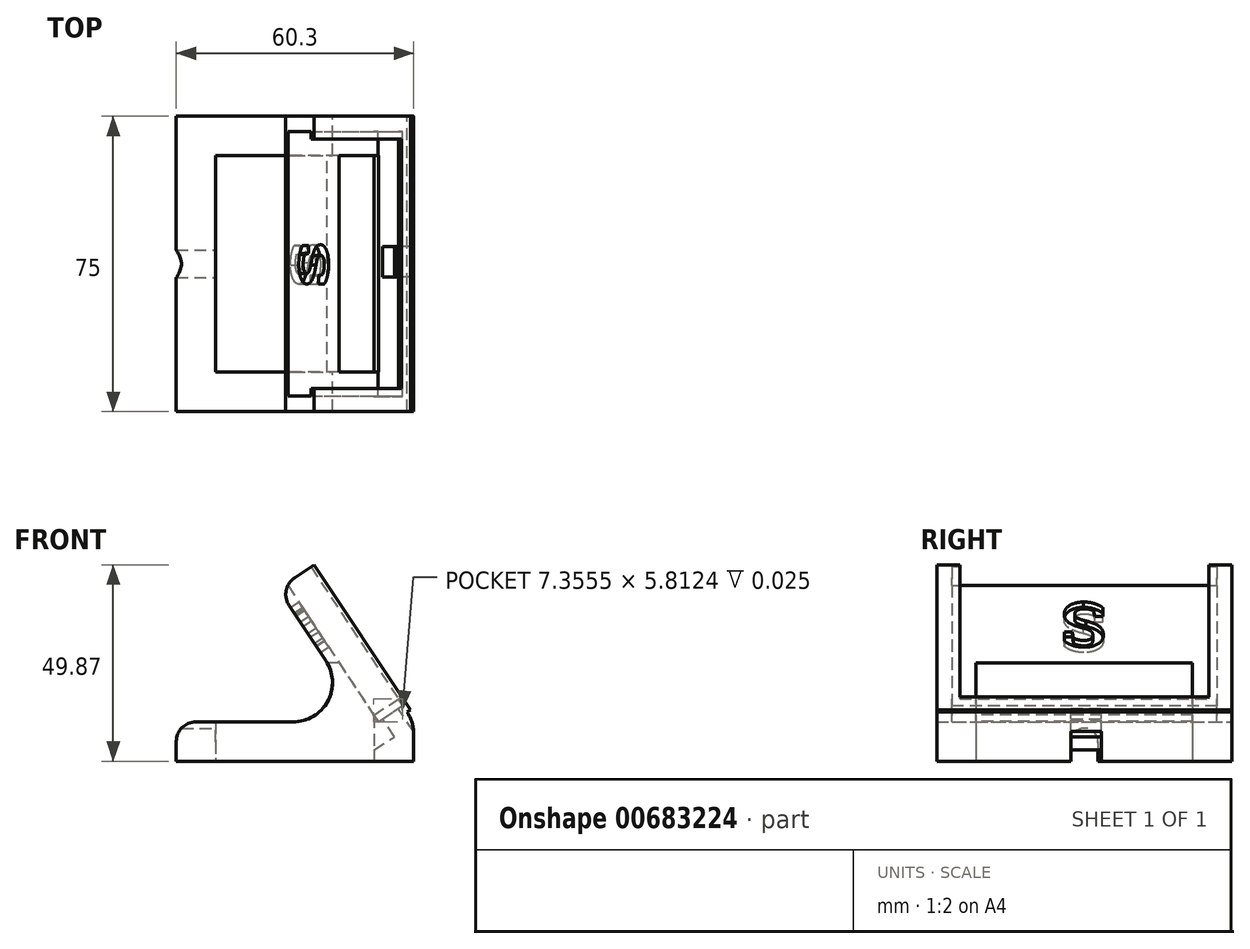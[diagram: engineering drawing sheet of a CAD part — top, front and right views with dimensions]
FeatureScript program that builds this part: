
annotation { "Feature Type Name" : "Feature", "Feature Type Description" : "" }
export const myFeature = defineFeature(function(context is Context, id is Id, definition is map)
    precondition{}
    {
        {
            var Q0;
            Q0=qCreatedBy(makeId("Front.planeOp"),FACE);
            var sketch = newSketch(context, id + "F0", { "sketchPlane" : qUnion([Q0])});
            skLineSegment(sketch, "E0", {"start": v(-43.3, 0) * mm, "end": v(-18.63, 0) * mm});
            skLineSegment(sketch, "E1", {"start": v(-10.3, 15.53) * mm, "end": v(-19.65, 29.62) * mm});
            skLineSegment(sketch, "E2", {"start": v(-18.25, 36.55) * mm, "end": v(-14.08, 39.32) * mm});
            skLineSegment(sketch, "E3", {"start": v(-14.08, 39.32) * mm, "end": v(10.33, 2.51) * mm});
            skLineSegment(sketch, "E4", {"start": v(12, -3.02) * mm, "end": v(12, -10) * mm});
            skLineSegment(sketch, "E5", {"start": v(12, -10) * mm, "end": v(-48.3, -10) * mm});
            skLineSegment(sketch, "E6", {"start": v(-48.3, -10) * mm, "end": v(-48.3, -5) * mm});
            skPoint(sketch, "E7.visualSharp", {"position": v(-48.3, 0) * mm});
            skArc(sketch, "E7.filletArc", {"start": v(-43.3, 0) * mm, "mid": v(-46.84, -1.46) * mm, "end": v(-48.3, -5) * mm});
            skPoint(sketch, "E8.visualSharp", {"position": v(12, 0) * mm});
            skArc(sketch, "E8.filletArc", {"start": v(12, -3.02) * mm, "mid": v(11.57, -0.13) * mm, "end": v(10.33, 2.51) * mm});
            skPoint(sketch, "E9.visualSharp", {"position": v(0, 0) * mm});
            skArc(sketch, "E9.filletArc", {"start": v(-18.63, 0) * mm, "mid": v(-9.82, 5.27) * mm, "end": v(-10.3, 15.53) * mm});
            skPoint(sketch, "E10.visualSharp", {"position": v(-22.41, 33.79) * mm});
            skArc(sketch, "E10.filletArc", {"start": v(-18.25, 36.55) * mm, "mid": v(-20.38, 33.38) * mm, "end": v(-19.65, 29.62) * mm});
            skSolve(sketch);
        }
        {
            var Q0;
            Q0 = qSketchRegion(id + "F0", true);
            extrude(context, id + "F1", {"entities" : qUnion([Q0]), "depth" : 75 * mm, "offsetDistance" : 25 * mm});
        }
        {
            var Q0;
            Q0=makeQuery(id+"F1.opExtrude","SWEPT_FACE",FACE,{"disambiguationData":[OSD([sQuery(id+"F0.wireOp",EDGE,"E3")])]});
            var sketch = newSketch(context, id + "F2", { "sketchPlane" : qUnion([Q0])});
            skLineSegment(sketch, "E11.bottom", {"start": v(-71.15, 60.38) * mm, "end": v(-3.85, 60.38) * mm});
            skLineSegment(sketch, "E11.top", {"start": v(-71.15, 0.38) * mm, "end": v(-3.85, 0.38) * mm});
            skLineSegment(sketch, "E11.left", {"start": v(-71.15, 60.38) * mm, "end": v(-71.15, 0.38) * mm});
            skLineSegment(sketch, "E11.right", {"start": v(-3.85, 60.38) * mm, "end": v(-3.85, 0.38) * mm});
            skPoint(sketch, "E11.middle", {"position": v(-37.5, 30.38) * mm});
            skSolve(sketch);
        }
        {
            var Q0;
            Q0 = qSketchRegion(id + "F2", true);
            extrude(context, id + "F3", {"entities" : qUnion([Q0]), "operationType" : NewBodyOperationType.REMOVE, "oppositeDirection" : true, "depth" : 7.5 * mm, "offsetDistance" : 25 * mm});
        }
        {
            var Q0;
            Q0=makeQuery(id+"F1.opExtrude","SWEPT_FACE",FACE,{"disambiguationData":[OSD([sQuery(id+"F0.wireOp",EDGE,"E5")])]});
            var sketch = newSketch(context, id + "F4", { "sketchPlane" : qUnion([Q0])});
            skLineSegment(sketch, "E12.bottom", {"start": v(2, 10) * mm, "end": v(-38.3, 10) * mm});
            skLineSegment(sketch, "E12.top", {"start": v(2, 65) * mm, "end": v(-38.3, 65) * mm});
            skLineSegment(sketch, "E12.left", {"start": v(2, 10) * mm, "end": v(2, 65) * mm});
            skLineSegment(sketch, "E12.right", {"start": v(-38.3, 10) * mm, "end": v(-38.3, 65) * mm});
            skPoint(sketch, "E12.middle", {"position": v(-18.15, 37.5) * mm});
            skSolve(sketch);
        }
        {
            var Q0;
            Q0 = qSketchRegion(id + "F4", true);
            extrude(context, id + "F5", {"entities" : qUnion([Q0]), "operationType" : NewBodyOperationType.REMOVE, "oppositeDirection" : true, "depth" : 25 * mm, "offsetDistance" : 25 * mm});
        }
        {
            var Q0;
            Q0=makeQuery(id+"F3.boolean.opBoolean","COPY",FACE,{"derivedFrom":makeQuery(id+"F3.opExtrude","SWEPT_FACE",FACE,{"disambiguationData":[OSD([sQuery(id+"F2.wireOp",EDGE,"E11.top")])]})});
            var sketch = newSketch(context, id + "F6", { "sketchPlane" : qUnion([Q0])});
            skLineSegment(sketch, "E13.bottom", {"start": v(3.83, -40.9) * mm, "end": v(8.63, -40.9) * mm});
            skLineSegment(sketch, "E13.top", {"start": v(3.83, -33.1) * mm, "end": v(8.63, -33.1) * mm});
            skLineSegment(sketch, "E13.left", {"start": v(3.83, -40.9) * mm, "end": v(3.83, -33.1) * mm});
            skLineSegment(sketch, "E13.right", {"start": v(8.63, -40.9) * mm, "end": v(8.63, -33.1) * mm});
            skPoint(sketch, "E13.middle", {"position": v(6.23, -37) * mm});
            skSolve(sketch);
        }
        {
            var Q0;
            Q0=makeQuery(id+"F6.imprint","IMPRINT",FACE,{"disambiguationData":[TD([[makeQuery(id+"F6.imprint","IMPRINT",EDGE,{"derivedFrom":sQuery(id+"F6.wireOp",EDGE,"E13.bottom")}),1.0]])]});
            extrude(context, id + "F7", {"entities" : qUnion([Q0]), "operationType" : NewBodyOperationType.REMOVE, "oppositeDirection" : true, "depth" : 25 * mm, "offsetDistance" : 25 * mm});
        }
        {
            var Q0;
            Q0=makeQuery(id+"F7.boolean.opBoolean","COPY",FACE,{"derivedFrom":makeQuery(id+"F7.opExtrude","SWEPT_FACE",FACE,{"disambiguationData":[OSD([sQuery(id+"F6.wireOp",EDGE,"E13.left")])]})});
            var sketch = newSketch(context, id + "F8", { "sketchPlane" : qUnion([Q0])});
            skLineSegment(sketch, "E14.bottom", {"start": v(-40.9, -7.08) * mm, "end": v(-33.1, -7.08) * mm});
            skLineSegment(sketch, "E14.top", {"start": v(-40.9, -15.34) * mm, "end": v(-33.1, -15.34) * mm});
            skLineSegment(sketch, "E14.left", {"start": v(-40.9, -7.08) * mm, "end": v(-40.9, -15.34) * mm});
            skLineSegment(sketch, "E14.right", {"start": v(-33.1, -7.08) * mm, "end": v(-33.1, -15.34) * mm});
            skPoint(sketch, "E14.middle", {"position": v(-37, -11.21) * mm});
            skPoint(sketch, "E14.middle.positionSnap0", {"position": v(-37, -14.54) * mm});
            skPoint(sketch, "E14.centerSnap0", {"position": v(-37, -14.54) * mm});
            skSolve(sketch);
        }
        {
            var Q0;
            Q0 = qSketchRegion(id + "F8", true);
            extrude(context, id + "F9", {"entities" : qUnion([Q0]), "operationType" : NewBodyOperationType.REMOVE, "oppositeDirection" : true, "depth" : 100 * mm, "offsetDistance" : 25 * mm});
        }
        {
            var Q0;
            Q0=makeQuery(id+"F5.boolean.opBoolean","COPY",FACE,{"derivedFrom":makeQuery(id+"F5.opExtrude","SWEPT_FACE",FACE,{"disambiguationData":[OSD([sQuery(id+"F4.wireOp",EDGE,"E12.right")])]})});
            var sketch = newSketch(context, id + "F10", { "sketchPlane" : qUnion([Q0])});
            skLineSegment(sketch, "E15.top", {"start": v(-41, -10) * mm, "end": v(-34, -10) * mm});
            skLineSegment(sketch, "E15.left", {"start": v(-41, -5.1) * mm, "end": v(-41, -10) * mm});
            skLineSegment(sketch, "E15.right", {"start": v(-34, -5.1) * mm, "end": v(-34, -10) * mm});
            skPoint(sketch, "E15.middle", {"position": v(-37.5, -7.55) * mm});
            skPoint(sketch, "E15.middle.positionSnap0", {"position": v(-37.5, -10) * mm});
            skPoint(sketch, "E15.centerSnap0", {"position": v(-37.5, -10) * mm});
            skArc(sketch, "E16", {"start": v(-34, -5.1) * mm, "mid": v(-37.5, -1.6) * mm, "end": v(-41, -5.1) * mm});
            skSolve(sketch);
        }
        {
            var Q0;
            Q0 = qSketchRegion(id + "F10", true);
            extrude(context, id + "F11", {"entities" : qUnion([Q0]), "operationType" : NewBodyOperationType.REMOVE, "oppositeDirection" : true, "depth" : 25 * mm, "offsetDistance" : 25 * mm});
        }
        {
            var Q0;
            Q0=makeQuery(id+"F3.boolean.opBoolean","COPY",FACE,{"derivedFrom":makeQuery(id+"F3.opExtrude","SWEPT_FACE",FACE,{"disambiguationData":[OSD([sQuery(id+"F2.wireOp",EDGE,"E11.right")])]})});
            var Q1;
            Q1=makeQuery(id+"F3.boolean.opBoolean","COPY",FACE,{"derivedFrom":makeQuery(id+"F3.opExtrude","SWEPT_FACE",FACE,{"disambiguationData":[OSD([sQuery(id+"F2.wireOp",EDGE,"E11.left")])]})});
            extrude(context, id + "F12", {"entities" : qUnion([Q0, Q1]), "operationType" : NewBodyOperationType.ADD, "depth" : 2 * mm, "offsetDistance" : 25 * mm});
        }
        {
            var Q0;
            Q0=makeQuery(id+"F3.boolean.opBoolean","COPY",FACE,{"derivedFrom":makeQuery(id+"F3.opExtrude","SWEPT_FACE",FACE,{"disambiguationData":[OSD([sQuery(id+"F2.wireOp",EDGE,"E11.left")])]})});
            extrude(context, id + "F13", {"entities" : qUnion([Q0]), "operationType" : NewBodyOperationType.ADD, "depth" : 2 * mm, "offsetDistance" : 25 * mm});
        }
        {
            var Q0;
            Q0=makeQuery(id+"F3.boolean.opBoolean","COPY",FACE,{"derivedFrom":makeQuery(id+"F3.opExtrude","SWEPT_FACE",FACE,{"disambiguationData":[OSD([sQuery(id+"F2.wireOp",EDGE,"E11.top")])]})});
            extrude(context, id + "F14", {"entities" : qUnion([Q0]), "operationType" : NewBodyOperationType.ADD, "depth" : 2 * mm, "offsetDistance" : 25 * mm});
        }
        {
            var Q0;
            {var subQ0=sQuery(id+"F2.wireOp",EDGE,"E11.top");var subQ1=sQuery(id+"F2.wireOp",EDGE,"E11.left");var subQ2=sQuery(id+"F2.wireOp",EDGE,"E11.right");Q0=makeQuery(id+"F14.boolean.opBoolean","MERGE",FACE,{"derivedFrom":[makeQuery(id+"F13.boolean.opBoolean","MERGE",FACE,{"derivedFrom":[makeQuery(id+"F12.boolean.opBoolean","MERGE",FACE,{"derivedFrom":[makeQuery(id+"F1.opExtrude","SWEPT_FACE",FACE,{"disambiguationData":[OSD([sQuery(id+"F0.wireOp",EDGE,"E3")])]}),makeQuery(id+"F12.opExtrude","SWEPT_FACE",FACE,{"disambiguationData":[OSD([subQ2]),TDD([makeQuery(id+"F3.boolean.opBoolean","COPY",EDGE,{"derivedFrom":makeQuery(id+"F3.opExtrude","CAP_EDGE",EDGE,{"disambiguationData":[OSD([subQ2])],"isStart":true})})])]})]}),makeQuery(id+"F13.opExtrude","SWEPT_FACE",FACE,{"disambiguationData":[OSD([subQ1]),TDD([makeQuery(id+"F3.boolean.opBoolean","COPY",EDGE,{"derivedFrom":makeQuery(id+"F3.opExtrude","CAP_EDGE",EDGE,{"disambiguationData":[OSD([subQ1])],"isStart":true})})])]})]}),makeQuery(id+"F14.opExtrude","SWEPT_FACE",FACE,{"disambiguationData":[OSD([subQ0]),TDD([makeQuery(id+"F3.boolean.opBoolean","COPY",EDGE,{"derivedFrom":makeQuery(id+"F3.opExtrude","CAP_EDGE",EDGE,{"disambiguationData":[OSD([subQ0])],"isStart":true})})])]})]});}
            extrude(context, id + "F15", {"entities" : qUnion([Q0]), "operationType" : NewBodyOperationType.ADD, "depth" : 1 * mm, "offsetDistance" : 25 * mm});
        }
        {
            var Q0;
            {var subQ0=sQuery(id+"F2.wireOp",EDGE,"E11.top");Q0=makeQuery(id+"F15.boolean.opBoolean","MERGE",FACE,{"derivedFrom":[makeQuery(id+"F14.opExtrude","CAP_FACE",FACE,{"disambiguationData":[OSD([subQ0])],"isStart":false}),makeQuery(id+"F15.opExtrude","SWEPT_FACE",FACE,{"disambiguationData":[OSD([subQ0])]})]});}
            var sketch = newSketch(context, id + "F16", { "sketchPlane" : qUnion([Q0])});
            skLineSegment(sketch, "E17.bottom", {"start": v(2.5, -71.13) * mm, "end": v(10, -71.13) * mm});
            skLineSegment(sketch, "E17.top", {"start": v(2.5, -3.88) * mm, "end": v(10, -3.88) * mm});
            skLineSegment(sketch, "E17.left", {"start": v(2.5, -71.13) * mm, "end": v(2.5, -3.87) * mm});
            skLineSegment(sketch, "E17.right", {"start": v(10, -71.13) * mm, "end": v(10, -3.87) * mm});
            skSolve(sketch);
        }
        {
            var Q0;
            Q0 = qSketchRegion(id + "F16", true);
            extrude(context, id + "F17", {"entities" : qUnion([Q0]), "operationType" : NewBodyOperationType.REMOVE, "oppositeDirection" : true, "depth" : -100 * mm, "offsetDistance" : 25 * mm});
        }
        {
            var Q0;
            {var subQ0=sQuery(id+"F2.wireOp",EDGE,"E11.top");Q0=makeQuery(id+"F17.boolean.opBoolean","MERGE",FACE,{"derivedFrom":[makeQuery(id+"F15.boolean.opBoolean","MERGE",FACE,{"derivedFrom":[makeQuery(id+"F14.opExtrude","CAP_FACE",FACE,{"disambiguationData":[OSD([subQ0])],"isStart":false}),makeQuery(id+"F15.opExtrude","SWEPT_FACE",FACE,{"disambiguationData":[OSD([subQ0])]})]}),makeQuery(id+"F17.opExtrude","CAP_FACE",FACE,{"disambiguationData":[OSD([sQuery(id+"F16.wireOp",EDGE,"E17.bottom"),sQuery(id+"F16.wireOp",EDGE,"E17.top"),sQuery(id+"F16.wireOp",EDGE,"E17.left"),sQuery(id+"F16.wireOp",EDGE,"E17.right")])],"isStart":true})]});}
            extrude(context, id + "F18", {"entities" : qUnion([Q0]), "operationType" : NewBodyOperationType.REMOVE, "oppositeDirection" : true, "depth" : 2 * mm, "offsetDistance" : 25 * mm});
        }
        {
            var Q0;
            Q0=makeQuery(id+"F6.imprint","IMPRINT",FACE,{"disambiguationData":[TD([[makeQuery(id+"F6.imprint","IMPRINT",EDGE,{"derivedFrom":sQuery(id+"F6.wireOp",EDGE,"E13.bottom")}),-1.0]])]});
            extrude(context, id + "F19", {"entities" : qUnion([Q0]), "operationType" : NewBodyOperationType.REMOVE, "oppositeDirection" : true, "depth" : 2 * mm, "offsetDistance" : 25 * mm});
        }
        {
            var Q0;
            {var subQ0=sQuery(id+"F2.wireOp",EDGE,"E11.right");var subQ1=sQuery(id+"F2.wireOp",EDGE,"E11.left");var subQ2=sQuery(id+"F2.wireOp",EDGE,"E11.top");var subQ3=makeQuery(id+"F3.boolean.opBoolean","COPY",FACE,{"derivedFrom":makeQuery(id+"F3.opExtrude","CAP_FACE",FACE,{"disambiguationData":[OSD([sQuery(id+"F2.wireOp",EDGE,"E11.bottom"),subQ2,subQ1,subQ0])],"isStart":false})});var subQ5=makeQuery(id+"F3.boolean.opBoolean","COPY",EDGE,{"derivedFrom":makeQuery(id+"F3.opExtrude","CAP_EDGE",EDGE,{"disambiguationData":[OSD([subQ2])],"isStart":false})});var subQ6=makeQuery(id+"F5.boolean.opBoolean","SPLIT",EDGE,{"disambiguationData":[TD([makeQuery(id+"F3.boolean.opBoolean","COPY",FACE,{"derivedFrom":makeQuery(id+"F3.opExtrude","SWEPT_FACE",FACE,{"disambiguationData":[OSD([subQ0])]})})])],"derivedFrom":subQ5});var subQ7=makeQuery(id+"F5.boolean.opBoolean","SPLIT",EDGE,{"disambiguationData":[TD([makeQuery(id+"F3.boolean.opBoolean","COPY",FACE,{"derivedFrom":makeQuery(id+"F3.opExtrude","SWEPT_FACE",FACE,{"disambiguationData":[OSD([subQ1])]})})])],"derivedFrom":subQ5});var subQ8=sQuery(id+"F16.wireOp",EDGE,"E17.left");var subQ9=makeQuery(id+"F17.opExtrude","CAP_EDGE",EDGE,{"disambiguationData":[OSD([subQ8])],"isStart":true});Q0=makeQuery(id+"F19.boolean.opBoolean","MERGE",FACE,{"derivedFrom":[makeQuery(id+"F18.boolean.opBoolean","MERGE",FACE,{"derivedFrom":[makeQuery(id+"F17.boolean.opBoolean","MERGE",FACE,{"derivedFrom":[subQ3,makeQuery(id+"F17.opExtrude","SWEPT_FACE",FACE,{"disambiguationData":[OSD([subQ8])]})]}),makeQuery(id+"F18.opExtrude","SWEPT_FACE",FACE,{"disambiguationData":[OSD([subQ2,subQ8]),TDD([makeQuery(id+"F17.boolean.opBoolean","MERGE",EDGE,{"derivedFrom":[makeQuery(id+"F14.opExtrude","CAP_EDGE",EDGE,{"disambiguationData":[OSD([subQ2]),TDD([subQ6])],"isStart":false}),subQ9]})])]}),makeQuery(id+"F18.opExtrude","SWEPT_FACE",FACE,{"disambiguationData":[OSD([subQ2,subQ8]),TDD([makeQuery(id+"F17.boolean.opBoolean","MERGE",EDGE,{"derivedFrom":[makeQuery(id+"F14.opExtrude","CAP_EDGE",EDGE,{"disambiguationData":[OSD([subQ2]),TDD([subQ7])],"isStart":false}),subQ9]})])]})]}),makeQuery(id+"F19.opExtrude","SWEPT_FACE",FACE,{"disambiguationData":[OSD([subQ2]),TDD([makeQuery(id+"F6.imprint","IMPRINT",EDGE,{"derivedFrom":subQ7})])]}),makeQuery(id+"F19.opExtrude","SWEPT_FACE",FACE,{"disambiguationData":[OSD([subQ2]),TDD([makeQuery(id+"F6.imprint","IMPRINT",EDGE,{"derivedFrom":subQ6})])]})]});}
            var sketch = newSketch(context, id + "F20", { "sketchPlane" : qUnion([Q0])});
            skText(sketch, "E18", { "text": "S", "fontName": "RobotoSlab-Bold.ttf"});
            const initialGuessF20  = {"E18": [-0.0435, 0.02134, 1, 0, 0.01354]};
            skSetInitialGuess(sketch, initialGuessF20);
            skSolve(sketch);
        }
        {
            var Q0;
            Q0 = qSketchRegion(id + "F20", true);
            extrude(context, id + "F21", {"entities" : qUnion([Q0]), "operationType" : NewBodyOperationType.REMOVE, "oppositeDirection" : true, "depth" : 25 * mm, "offsetDistance" : 25 * mm});
        }
    });
